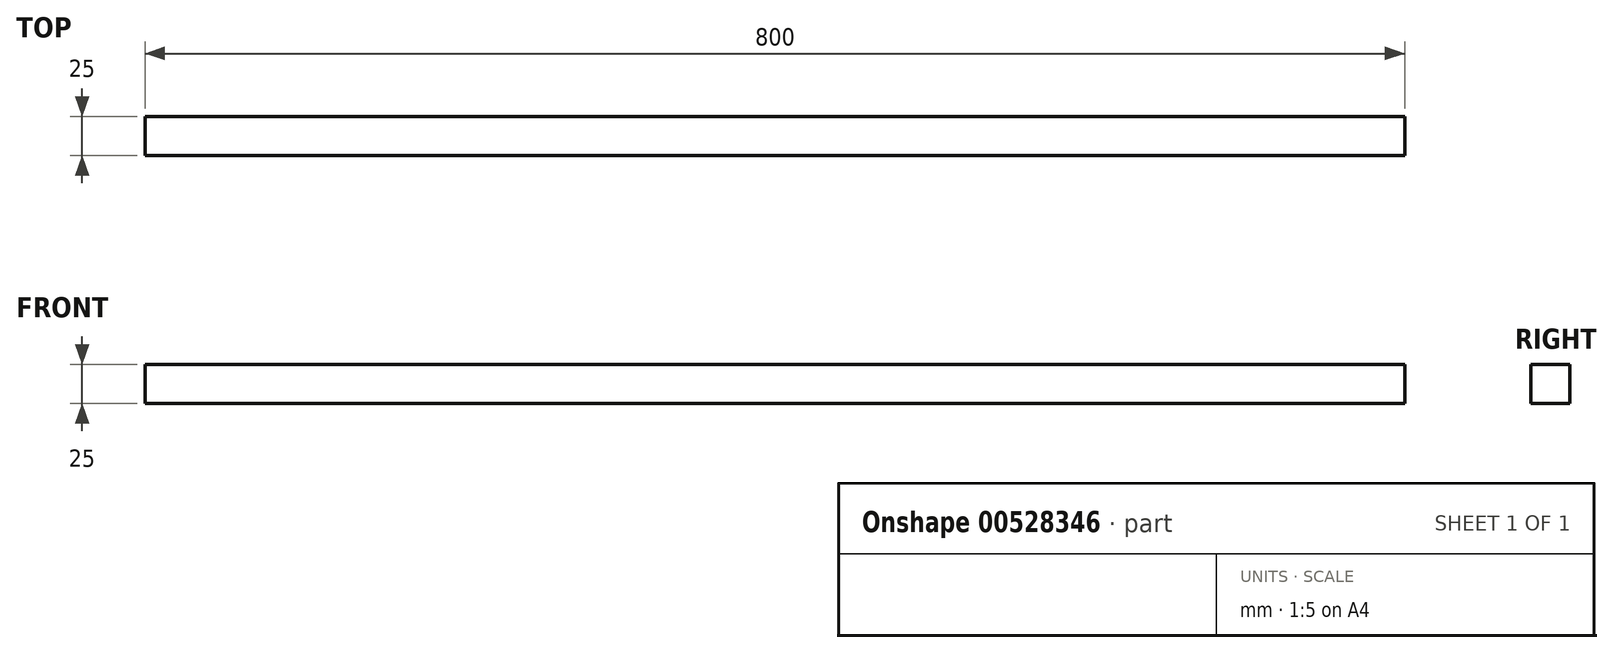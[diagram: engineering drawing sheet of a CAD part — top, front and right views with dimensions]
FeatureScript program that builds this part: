
annotation { "Feature Type Name" : "Feature", "Feature Type Description" : "" }
export const myFeature = defineFeature(function(context is Context, id is Id, definition is map)
    precondition{}
    {
        {
            var Q0;
            Q0=qCreatedBy(makeId("Top.planeOp"),FACE);
            var sketch = newSketch(context, id + "F0", { "sketchPlane" : qUnion([Q0])});
            skLineSegment(sketch, "E0.bottom", {"start": v(400, -12.5) * mm, "end": v(-400, -12.5) * mm});
            skLineSegment(sketch, "E0.top", {"start": v(400, 12.5) * mm, "end": v(-400, 12.5) * mm});
            skLineSegment(sketch, "E0.left", {"start": v(400, -12.5) * mm, "end": v(400, 12.5) * mm});
            skLineSegment(sketch, "E0.right", {"start": v(-400, -12.5) * mm, "end": v(-400, 12.5) * mm});
            skPoint(sketch, "E0.middle", {"position": v(0, 0) * mm});
            skSolve(sketch);
        }
        {
            var Q0;
            Q0=makeQuery(id+"F0.imprint","IMPRINT",FACE,{"disambiguationData":[TD([[makeQuery(id+"F0.imprint","IMPRINT",EDGE,{"derivedFrom":sQuery(id+"F0.wireOp",EDGE,"E0.bottom")}),-1.0]])]});
            extrude(context, id + "F1", {"entities" : qUnion([Q0]), "depth" : 25 * mm, "offsetDistance" : 25 * mm});
        }
    });
